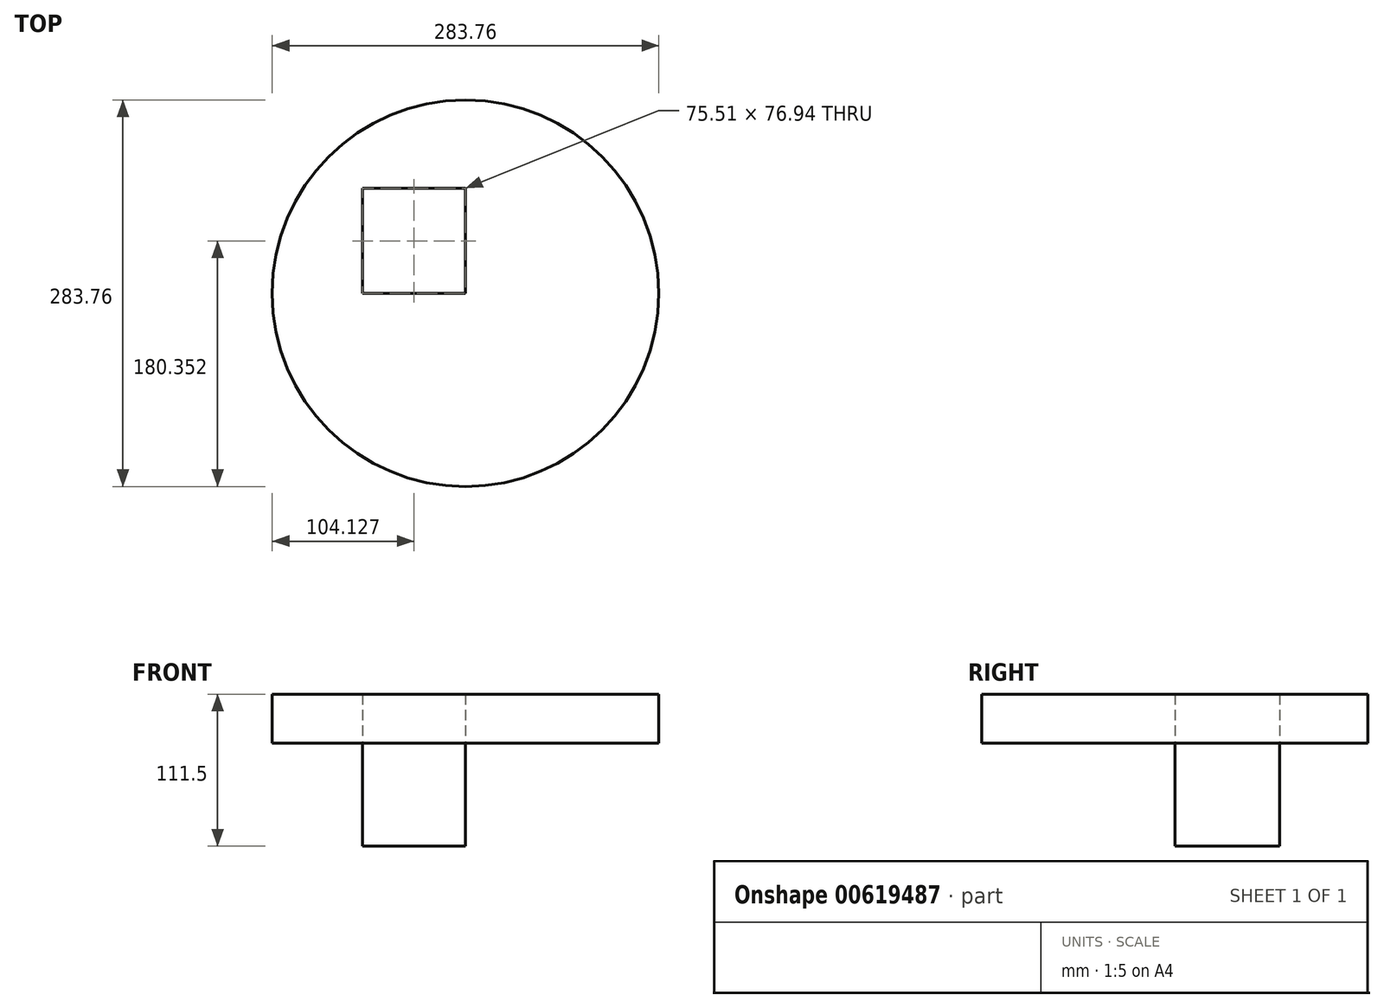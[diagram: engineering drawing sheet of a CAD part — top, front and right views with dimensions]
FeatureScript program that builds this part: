
annotation { "Feature Type Name" : "Feature", "Feature Type Description" : "" }
export const myFeature = defineFeature(function(context is Context, id is Id, definition is map)
    precondition{}
    {
        {
            var Q0;
            Q0=qCreatedBy(makeId("Top.planeOp"),FACE);
            var sketch = newSketch(context, id + "F0", { "sketchPlane" : qUnion([Q0])});
            skLineSegment(sketch, "E0.bottom", {"start": v(0, 0) * mm, "end": v(-75.5, 0) * mm});
            skLineSegment(sketch, "E0.top", {"start": v(0, 76.94) * mm, "end": v(-75.5, 76.94) * mm});
            skLineSegment(sketch, "E0.left", {"start": v(0, 0) * mm, "end": v(0, 76.94) * mm});
            skLineSegment(sketch, "E0.right", {"start": v(-75.5, 0) * mm, "end": v(-75.5, 76.94) * mm});
            skSolve(sketch);
        }
        {
            var Q0;
            Q0=makeQuery(id+"F0.imprint","IMPRINT",FACE,{"disambiguationData":[TD([[makeQuery(id+"F0.imprint","IMPRINT",EDGE,{"derivedFrom":sQuery(id+"F0.wireOp",EDGE,"E0.bottom")}),-1.0]])]});
            extrude(context, id + "F1", {"entities" : qUnion([Q0]), "oppositeDirection" : true, "depth" : 75.7 * mm, "offsetDistance" : 25.4 * mm});
        }
        {
            var Q0;
            Q0=makeQuery(id+"F1.opExtrude","CAP_FACE",FACE,{"disambiguationData":[OSD([sQuery(id+"F0.wireOp",EDGE,"E0.bottom"),sQuery(id+"F0.wireOp",EDGE,"E0.top"),sQuery(id+"F0.wireOp",EDGE,"E0.left"),sQuery(id+"F0.wireOp",EDGE,"E0.right")])],"isStart":true});
            var sketch = newSketch(context, id + "F2", { "sketchPlane" : qUnion([Q0])});
            skCircle(sketch, "E1", {"center": v(0, 0) * mm, "radius": 141.88 * mm});
            skSolve(sketch);
        }
        {
            var Q0;
            Q0=makeQuery(id+"F2.imprint","IMPRINT",FACE,{"disambiguationData":[TD([[makeQuery(id+"F2.imprint","IMPRINT",EDGE,{"derivedFrom":sQuery(id+"F2.wireOp",EDGE,"E1")}),1.0]])]});
            extrude(context, id + "F3", {"entities" : qUnion([Q0]), "depth" : 35.81 * mm, "offsetDistance" : 25.4 * mm});
        }
        {
            var Q0;
            Q0=makeQuery(id+"F3.opExtrude","CAP_FACE",FACE,{"disambiguationData":[OSD([sQuery(id+"F0.wireOp",EDGE,"E0.bottom"),sQuery(id+"F0.wireOp",EDGE,"E0.top"),sQuery(id+"F0.wireOp",EDGE,"E0.left"),sQuery(id+"F0.wireOp",EDGE,"E0.right"),sQuery(id+"F2.wireOp",EDGE,"E1")])],"isStart":true});
            var sketch = newSketch(context, id + "F4", { "sketchPlane" : qUnion([Q0])});
            skLineSegment(sketch, "E2.bottom", {"start": v(0, 0) * mm, "end": v(74.15, 0) * mm});
            skLineSegment(sketch, "E2.top", {"start": v(0, -74.95) * mm, "end": v(74.15, -74.95) * mm});
            skLineSegment(sketch, "E2.left", {"start": v(0, 0) * mm, "end": v(0, -74.95) * mm});
            skLineSegment(sketch, "E2.right", {"start": v(74.15, 0) * mm, "end": v(74.15, -74.95) * mm});
            skLineSegment(sketch, "E3.top", {"start": v(0, 76.23) * mm, "end": v(74.15, 76.23) * mm});
            skLineSegment(sketch, "E3.left", {"start": v(0, 0) * mm, "end": v(0, 76.23) * mm});
            skLineSegment(sketch, "E3.right", {"start": v(74.15, 0) * mm, "end": v(74.15, 76.23) * mm});
            skLineSegment(sketch, "E4.bottom", {"start": v(0, 0) * mm, "end": v(-75.55, 0) * mm});
            skLineSegment(sketch, "E4.top", {"start": v(0, 76.23) * mm, "end": v(-75.55, 76.23) * mm});
            skLineSegment(sketch, "E4.right", {"start": v(-75.55, 0) * mm, "end": v(-75.55, 76.23) * mm});
            skSolve(sketch);
        }
        {
            var Q0;
            Q0=makeQuery(id+"F4.imprint","IMPRINT",FACE,{"disambiguationData":[TD([[makeQuery(id+"F4.imprint","IMPRINT",EDGE,{"derivedFrom":sQuery(id+"F4.wireOp",EDGE,"E4.top")}),1.0]])]});
            var Q1;
            Q1=makeQuery(id+"F4.imprint","IMPRINT",FACE,{"disambiguationData":[TD([[makeQuery(id+"F4.imprint","IMPRINT",EDGE,{"derivedFrom":sQuery(id+"F4.wireOp",EDGE,"E2.bottom")}),1.0]])]});
            extrude(context, id + "F5", {"entities" : qUnion([Q0, Q1]), "operationType" : NewBodyOperationType.ADD, "oppositeDirection" : true, "depth" : 25.4 * mm, "offsetDistance" : 25.4 * mm});
        }
    });
